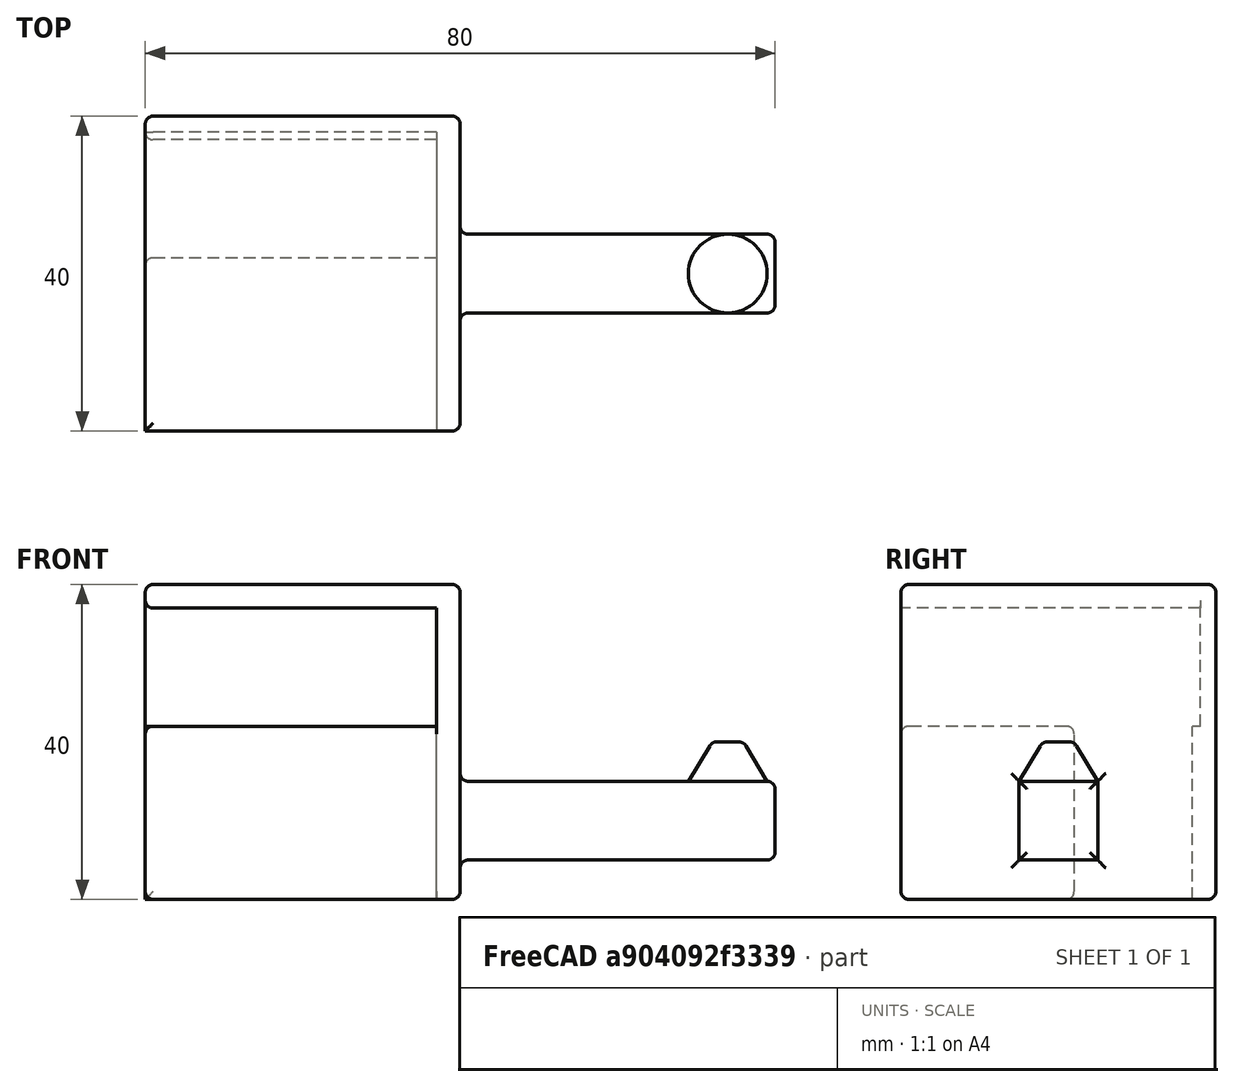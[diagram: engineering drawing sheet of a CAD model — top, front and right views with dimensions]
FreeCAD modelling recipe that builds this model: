
FCSTD DOCUMENT  (FreeCAD 0.20R28811 (Git))
Label: Penja_Auriculars_Cantoner
License: All rights reserved
LicenseURL: http://en.wikipedia.org/wiki/All_rights_reserved
objects: Part::Fillet×13, Part::Box×4, Part::Cut×2, Part::MultiFuse×2, Part::Cone×1
note: 22 computed .brp shape members not serialized (recipe doc carries the construction recipe); baked Part::Feature solids carry a one-line shape summary decoded from their .brp

FEATURE [Part::Box] Box  label="Cube"
  AttacherType = Attacher::AttachEngine3D
  Height = 40
  Length = 40
  Width = 40
FEATURE [Part::Box] Box001  label="Cube001"
  AttacherType = Attacher::AttachEngine3D
  Height = 15
  Length = 39
  Placement = pos=(3,2,22) rot=(0,0,1;0rad)
  Width = 39
FEATURE [Part::Box] Box002  label="Cube002"
  AttacherType = Attacher::AttachEngine3D
  Height = 37
  Length = 39
  Placement = pos=(3,3,0) rot=(0,0,1;0rad)
  Width = 15
FEATURE [Part::Cut] Cut
  Base = -> Box
  Refine = true
  Tool = -> Box001
FEATURE [Part::Cut] Cut001
  Base = -> Cut
  Refine = true
  Tool = -> Box002
FEATURE [Part::Fillet] Fillet
  Base = -> Cut001
  Edges = 1 edges r=1: [Edge28]
FEATURE [Part::Fillet] Fillet001
  Base = -> Fillet
  Edges = 1 edges r=1: [Edge6]
FEATURE [Part::Fillet] Fillet002
  Base = -> Fillet001
  Edges = 2 edges r=1: [Edge14,Edge22]
FEATURE [Part::Fillet] Fillet003
  Base = -> Fillet002
  Edges = 8 edges r=1: [Edge11,Edge21,Edge22,Edge35,Edge36,Edge41,Edge42,Edge47]
FEATURE [Part::Fillet] Fillet004
  Base = -> Fillet003
  Edges = 1 edges r=1: [Edge30]
FEATURE [Part::Fillet] Fillet005
  Base = -> Fillet004
  Edges = 1 edges r=1: [Edge13]
FEATURE [Part::Fillet] Fillet006
  Base = -> Fillet005
  Edges = 4 edges r=1: [Edge14,Edge34,Edge56,Edge58]
  Placement = pos=(0,0,0) rot=(0,0,1;3.14159rad)
FEATURE [Part::Box] Box003  label="Cube003"
  AttacherType = Attacher::AttachEngine3D
  Height = 10
  Length = 40
  Placement = pos=(0,-25,5) rot=(0,0,1;0rad)
  Width = 10
FEATURE [Part::Cone] Cone
  Angle = 360
  AttacherType = Attacher::AttachEngine3D
  Height = 5
  Placement = pos=(35,-20,15) rot=(0,0,1;0rad)
  Radius1 = 5
  Radius2 = 2
FEATURE [Part::Fillet] Fillet007
  Base = -> Box003
  Edges = 4 edges r=1: [Edge5,Edge6,Edge7,Edge8]
FEATURE [Part::Fillet] Fillet008
  Base = -> Cone
  Edges = 1 edges r=1: [Edge1]
  Placement = pos=(-1,0,0) rot=(0,0,1;0rad)
FEATURE [Part::MultiFuse] Fusion
  Refine = true
  Shapes = -> [Fillet006,Fillet007]
FEATURE [Part::Fillet] Fillet009
  Base = -> Fusion
  Edges = 1 edges r=1: [Edge66]
FEATURE [Part::Fillet] Fillet010
  Base = -> Fillet009
  Edges = 1 edges r=1: [Edge4]
FEATURE [Part::Fillet] Fillet011
  Base = -> Fillet010
  Edges = 1 edges r=1: [Edge7]
FEATURE [Part::Fillet] Fillet012
  Base = -> Fillet011
  Edges = 1 edges r=1: [Edge2]
FEATURE [Part::MultiFuse] Fusion001
  Refine = true
  Shapes = -> [Fillet012,Fillet008]
